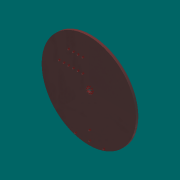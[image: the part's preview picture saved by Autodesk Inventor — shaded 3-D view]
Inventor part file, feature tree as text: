
AUTODESK INVENTOR PART (.ipt)
format: ipt  version: 2013 (Build 170138000, 138)  size: 147,968 bytes
history: native  units: mm
features: sketch x5, extrude x3, hole x2, other x1
ambient origin geometry x8: Origin, YZ Plane, XZ Plane, XY Plane, X Axis, Y Axis, Z Axis, Center Point
feature tree (11):
  other  "ソリッド1"
  extrude  "押し出し1"  Depth=200.0mm
  hole  "穴5"  [1 undecoded]
  extrude  "押し出し4"  Depth=8.0mm
  hole  "穴6"  [1 undecoded]
  extrude  "押し出し7"  Depth=12.0mm
  sketch  "スケッチ1"
  sketch  "スケッチ12"
  sketch  "スケッチ13"
  sketch  "スケッチ14"
  sketch  "スケッチ16"
note: 2 required parameter values undecoded (feature->parameter linkage not recoverable at this tier; creation-order binding heuristic only, values carry confidence <= 0.55)
